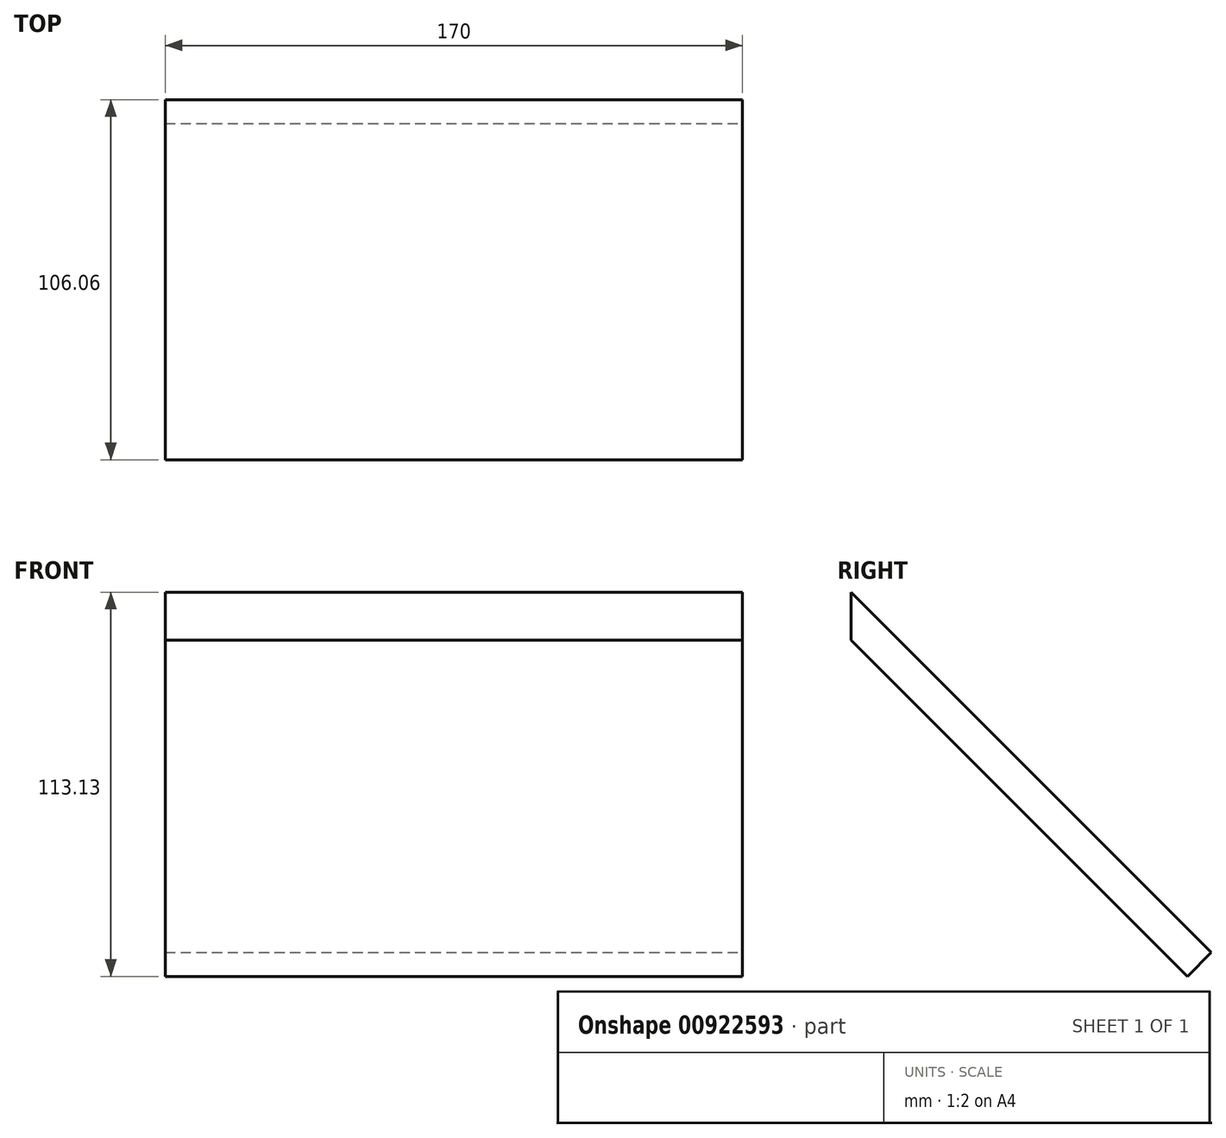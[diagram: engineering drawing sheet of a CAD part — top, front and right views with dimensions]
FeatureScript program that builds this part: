
annotation { "Feature Type Name" : "Feature", "Feature Type Description" : "" }
export const myFeature = defineFeature(function(context is Context, id is Id, definition is map)
    precondition{}
    {
        {
            var Q0;
            Q0=qCreatedBy(makeId("Top.planeOp"),FACE);
            var Q1;
            Q1=qCreatedBy(makeId("Front.planeOp"),FACE);
            cPlane(context, id + "F0", {"entities" : qUnion([Q0, Q1]), "cplaneType" : CPlaneType.MID_PLANE, "offset" : 25.4 * mm, "width" : 152.4 * mm, "height" : 152.4 * mm});
        }
        {
            var Q0;
            Q0=qCreatedBy(id+"F0.planeOp",FACE);
            var sketch = newSketch(context, id + "F1", { "sketchPlane" : qUnion([Q0])});
            skLineSegment(sketch, "E0.bottom", {"start": v(85, 75) * mm, "end": v(-85, 75) * mm});
            skLineSegment(sketch, "E0.top", {"start": v(85, -75) * mm, "end": v(-85, -75) * mm});
            skLineSegment(sketch, "E0.left", {"start": v(85, 75) * mm, "end": v(85, -75) * mm});
            skLineSegment(sketch, "E0.right", {"start": v(-85, 75) * mm, "end": v(-85, -75) * mm});
            skPoint(sketch, "E0.middle", {"position": v(0, 0) * mm});
            skSolve(sketch);
        }
        {
            var Q0;
            Q0 = qSketchRegion(id + "F1", true);
            extrude(context, id + "F2", {"entities" : qUnion([Q0]), "depth" : 10 * mm, "offsetDistance" : 25.4 * mm});
        }
        {
            var Q0;
            Q0=makeQuery(id+"F2.opExtrude","CAP_EDGE",EDGE,{"disambiguationData":[OSD([sQuery(id+"F1.wireOp",EDGE,"E0.bottom")])],"isStart":true});
            chamfer(context, id + "F3", {"entities" : qUnion([Q0]), "width" : 10 * mm, "tangentPropagation" : true});
        }
    });
